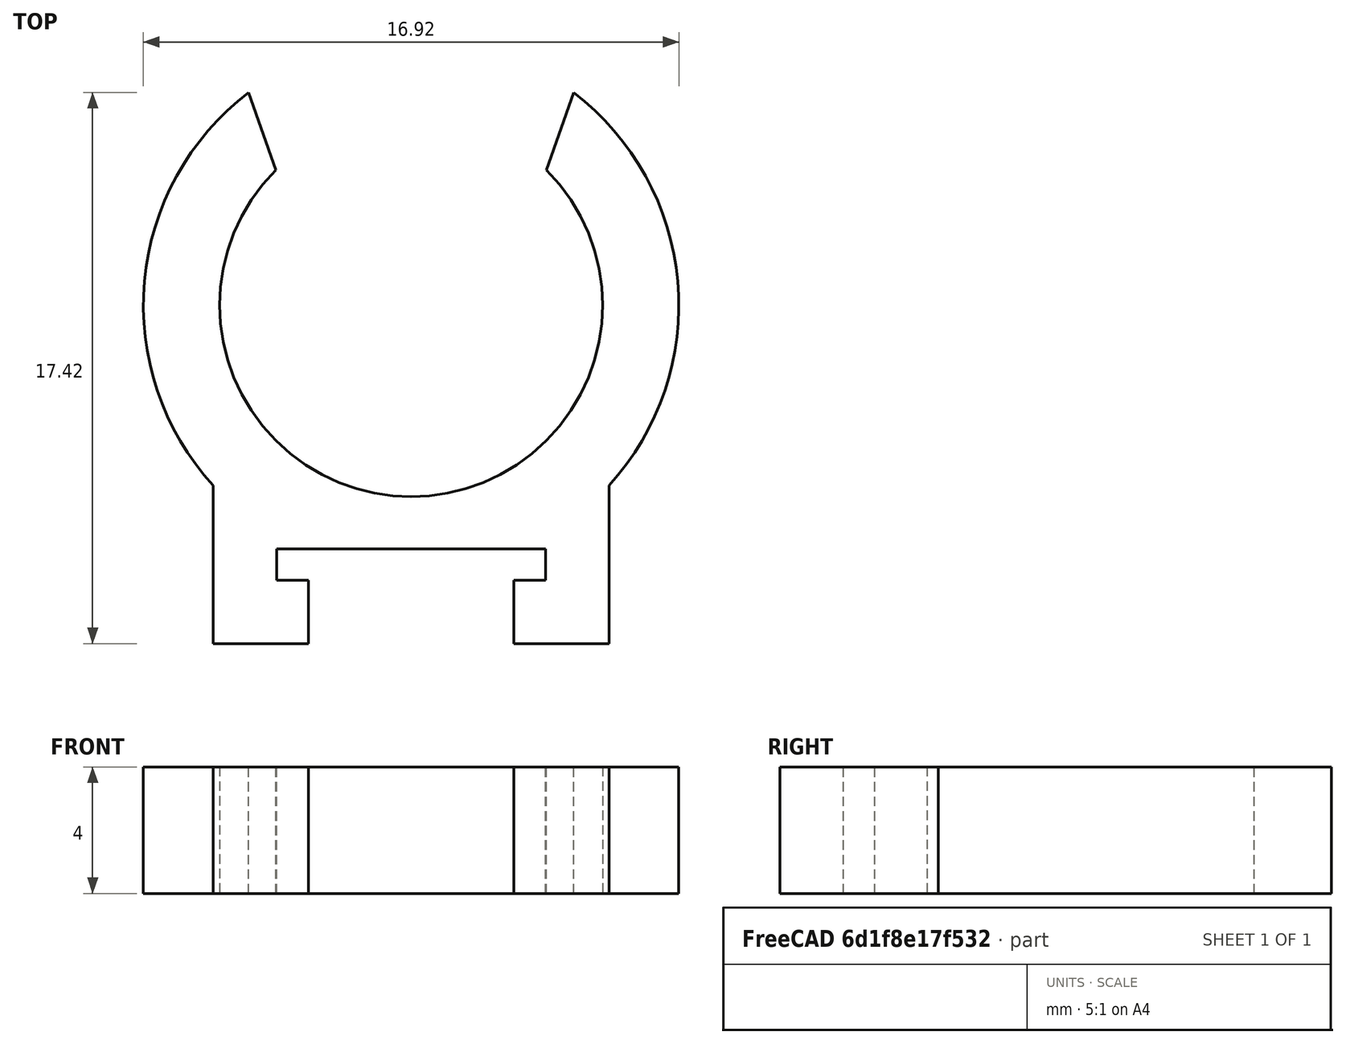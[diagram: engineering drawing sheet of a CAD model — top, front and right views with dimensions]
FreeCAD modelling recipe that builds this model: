
FCSTD DOCUMENT  (FreeCAD 0.20R29177 +426 (Git))
Label: 8mm_strip_led_to_12mm_diameter_clamp
Comment: Created to attach an 8mm LED strip to a 12mm diameter rod used for framing an 3d printer enclosure
License: Creative Commons Attribution
LicenseURL: http://creativecommons.org/licenses/by/4.0/
objects: Sketcher::SketchObject×1, PartDesign::Pad×1, PartDesign::Body×1
note: 4 computed .brp shape members not serialized (recipe doc carries the construction recipe); baked Part::Feature solids carry a one-line shape summary decoded from their .brp

FEATURE [Sketcher::SketchObject] Sketch
  FullyConstrained = false
  MapMode = 5
  Support = -> [XY_Plane]
  sketch-geometry (16):
    g0: LineSegment StartX=-6.25 StartY=-6.24398 StartZ=0 EndX=-6.25 EndY=-11.244 EndZ=0
    g1: LineSegment StartX=-6.25 StartY=-11.244 StartZ=0 EndX=-3.25 EndY=-11.244 EndZ=0
    g2: LineSegment StartX=-3.25 StartY=-11.244 StartZ=0 EndX=-3.25 EndY=-9.24398 EndZ=0
    g3: LineSegment StartX=-3.25 StartY=-9.24398 StartZ=0 EndX=-4.25 EndY=-9.24398 EndZ=0
    g4: LineSegment StartX=-4.25 StartY=-9.24398 StartZ=0 EndX=-4.25 EndY=-8.24398 EndZ=0
    g5: LineSegment StartX=-4.25 StartY=-8.24398 StartZ=0 EndX=4.25 EndY=-8.24398 EndZ=0
    g6: LineSegment StartX=4.25 StartY=-8.24398 StartZ=0 EndX=4.25 EndY=-9.24398 EndZ=0
    g7: LineSegment StartX=4.25 StartY=-9.24398 StartZ=0 EndX=3.25 EndY=-9.24398 EndZ=0
    g8: LineSegment StartX=3.25 StartY=-9.24398 StartZ=0 EndX=3.25 EndY=-11.244 EndZ=0
    g9: LineSegment StartX=3.25 StartY=-11.244 StartZ=0 EndX=6.25 EndY=-11.244 EndZ=0
    g10: LineSegment StartX=6.25 StartY=-11.244 StartZ=0 EndX=6.25 EndY=-6.24398 EndZ=0
    g11: ArcOfCircle CenterX=0 CenterY=-0.544275 CenterZ=0 NormalX=0 NormalY=0 NormalZ=1 AngleXU=0 Radius=8.45867 StartAngle=5.54381 EndAngle=7.20187
    g12: ArcOfCircle CenterX=0 CenterY=-0.544275 CenterZ=0 NormalX=0 NormalY=0 NormalZ=1 AngleXU=0 Radius=8.45867 StartAngle=2.22291 EndAngle=3.88097
    g13: ArcOfCircle CenterX=0 CenterY=-0.544275 CenterZ=0 NormalX=0 NormalY=0 NormalZ=1 AngleXU=0 Radius=6.05 StartAngle=2.35619 EndAngle=7.06858
    g14: LineSegment StartX=4.278 StartY=3.73372 StartZ=0 EndX=5.13329 EndY=6.1787 EndZ=0
    g15: LineSegment StartX=-4.278 StartY=3.73372 StartZ=0 EndX=-5.13329 EndY=6.1787 EndZ=0
  constraints (47):
    c: Vertical(g0)
    c: Coincident(g0,g1)
    c: Horizontal(g1)
    c: Coincident(g1,g2)
    c: Coincident(g2,g3)
    c: Coincident(g3,g4)
    c: Coincident(g4,g5)
    c: Horizontal(g5)
    c: Coincident(g5,g6)
    c: Coincident(g6,g7)
    c: Horizontal(g7)
    c: Coincident(g7,g8)
    c: Vertical(g8)
    c: Coincident(g8,g9)
    c: Horizontal(g9)
    c: Coincident(g9,g10)
    c: PointOnObject(g11,g-2)
    c: Vertical(g10)
    c: Equal(g2,g8)
    c: Vertical(g2)
    c: Equal(g1,g9)
    c: Equal(g4,g6)  'Led lip equals'
    c: Horizontal(g3)
    c: Vertical(g4)
    c: Vertical(g6)
    c: Equal(g10,g0)
    c: Equal(g7,g3)
    c: Coincident(g14,g11)
    c: Equal(g15,g14)
    c: Coincident(g15,g12)
    c: Coincident(g15,g13)
    c: Coincident(g14,g13)
    c: Coincident(g11,g12)
    c: Diameter(g13) = 12.1  'Inner diameter'
    c: DistanceY(g6,g6) = 1
    c: DistanceX(g5,g5) = 8.5  'Led Strip Width'
    c: DistanceY(g10,g10) = 5
    c: DistanceY(g8,g8) = 2
    c: DistanceX(g9,g9) = 3  'Led Overhang'
    c: Angle(g13) = 4.71239  'Tube Clip angle'
    c: Coincident(g13,g11)
    c: Angle(g12) = 1.65806
    c: Horizontal(g13,g13)
    c: Horizontal(g12,g11)
    c: Coincident(g12,g0)
    c: Coincident(g10,g11)
    c: DistanceX(g3,g3) = 1  'Lip grip overlap'
FEATURE [PartDesign::Pad] Pad
  Direction = (0,0,1)
  Length = 4
  Length2 = 10
  Profile = -> Sketch
  ReferenceAxis = -> Sketch [N_Axis]
  Type = 0
FEATURE [PartDesign::Body] Body
  Group = -> [Sketch,Pad]
  Origin = -> Origin
  Tip = -> Pad
